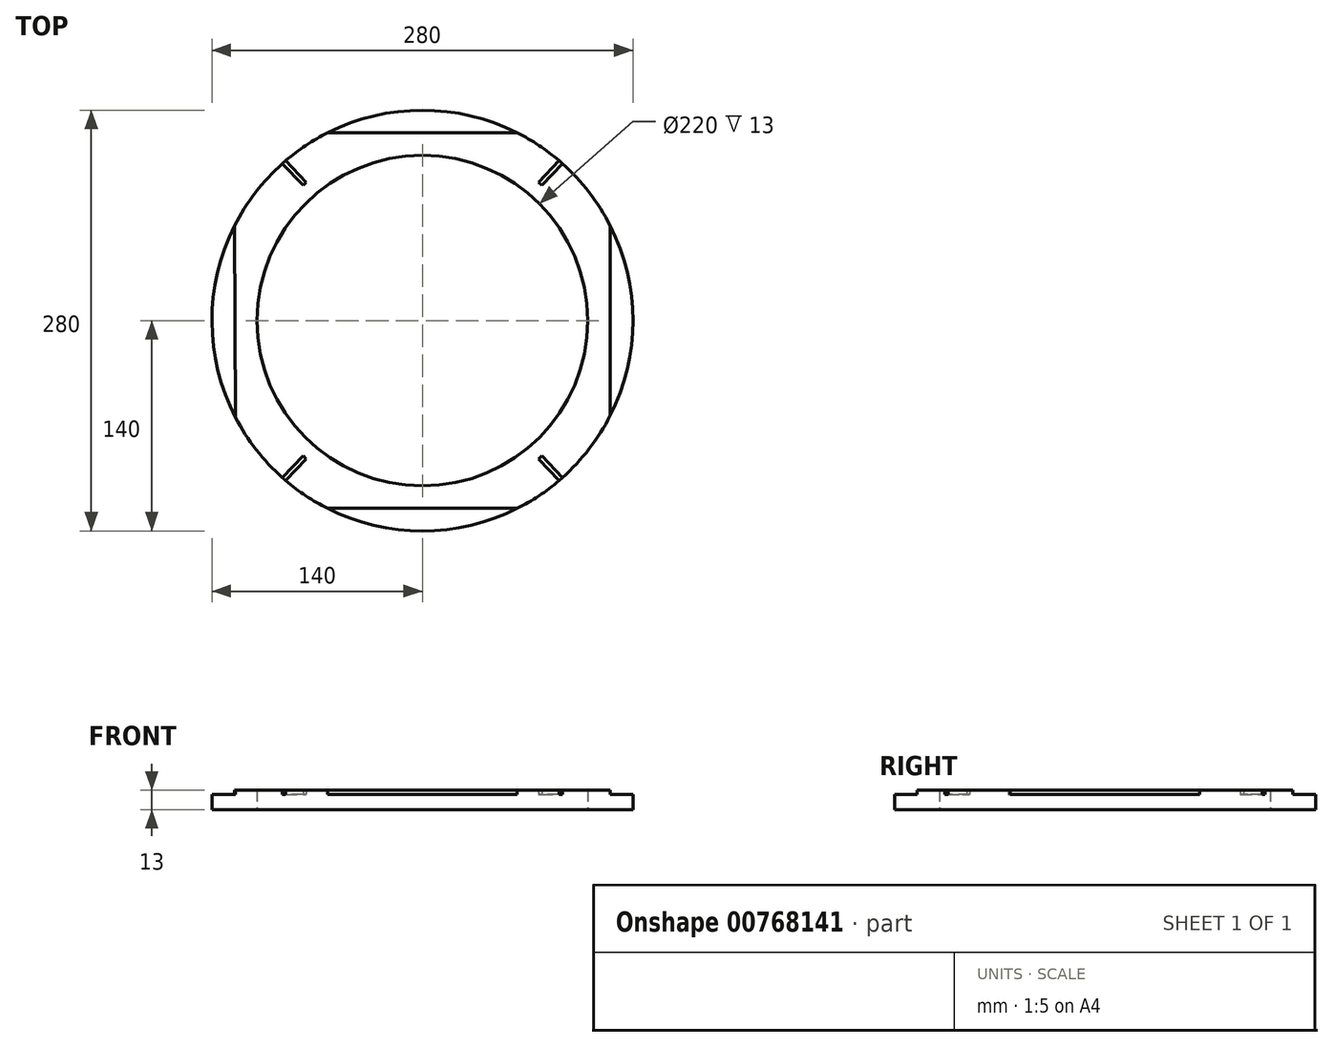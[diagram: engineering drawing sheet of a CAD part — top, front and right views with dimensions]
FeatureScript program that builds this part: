
annotation { "Feature Type Name" : "Feature", "Feature Type Description" : "" }
export const myFeature = defineFeature(function(context is Context, id is Id, definition is map)
    precondition{}
    {
        {
            var Q0;
            Q0=qCreatedBy(makeId("Top.planeOp"),FACE);
            var sketch = newSketch(context, id + "F0", { "sketchPlane" : qUnion([Q0])});
            skCircle(sketch, "E0", {"center": v(0, 0) * mm, "radius": 140 * mm});
            skCircle(sketch, "E1", {"center": v(0, 0) * mm, "radius": 110 * mm});
            skLineSegment(sketch, "E2", {"start": v(-93.13, 104.53) * mm, "end": v(-79.37, 90.02) * mm});
            skLineSegment(sketch, "E3", {"start": v(-79.37, 90.02) * mm, "end": v(-77.2, 92.08) * mm});
            skLineSegment(sketch, "E4", {"start": v(-77.2, 92.08) * mm, "end": v(-90.87, 106.5) * mm});
            skLineSegment(sketch, "E5", {"start": v(-90.87, 106.5) * mm, "end": v(-93.13, 104.53) * mm});
            skLineSegment(sketch, "E6.MirrorCS", {"start": v(-77.2, -92.08) * mm, "end": v(-90.87, -106.5) * mm});
            skLineSegment(sketch, "E7.MirrorCS", {"start": v(-79.37, -90.02) * mm, "end": v(-77.2, -92.08) * mm});
            skLineSegment(sketch, "E8.MirrorCS", {"start": v(-90.87, -106.5) * mm, "end": v(-93.13, -104.53) * mm});
            skLineSegment(sketch, "E9.MirrorCS", {"start": v(-93.13, -104.53) * mm, "end": v(-79.37, -90.02) * mm});
            skLineSegment(sketch, "E10.MirrorCS", {"start": v(90.87, -106.5) * mm, "end": v(93.13, -104.53) * mm});
            skLineSegment(sketch, "E11.MirrorCS", {"start": v(79.37, -90.02) * mm, "end": v(77.2, -92.08) * mm});
            skLineSegment(sketch, "E12.MirrorCS", {"start": v(90.87, 106.5) * mm, "end": v(93.13, 104.53) * mm});
            skLineSegment(sketch, "E13.MirrorCS", {"start": v(79.37, 90.02) * mm, "end": v(77.2, 92.08) * mm});
            skLineSegment(sketch, "E14.MirrorCS", {"start": v(77.2, -92.08) * mm, "end": v(90.87, -106.5) * mm});
            skLineSegment(sketch, "E15.MirrorCS", {"start": v(77.2, 92.08) * mm, "end": v(90.87, 106.5) * mm});
            skLineSegment(sketch, "E16.MirrorCS", {"start": v(93.13, 104.53) * mm, "end": v(79.37, 90.02) * mm});
            skLineSegment(sketch, "E17.MirrorCS", {"start": v(93.13, -104.53) * mm, "end": v(79.37, -90.02) * mm});
            skLineSegment(sketch, "E18", {"start": v(0, 140) * mm, "end": v(0, 110) * mm});
            skLineSegment(sketch, "E19", {"start": v(110, 0) * mm, "end": v(140, 0) * mm});
            skLineSegment(sketch, "E20", {"start": v(-110, 0) * mm, "end": v(-140, 0) * mm});
            skLineSegment(sketch, "E21", {"start": v(0, -110) * mm, "end": v(0, -140) * mm});
            skLineSegment(sketch, "E22", {"start": v(0, 125) * mm, "end": v(63.05, 125) * mm});
            skLineSegment(sketch, "E23", {"start": v(63.05, 125) * mm, "end": v(-63.05, 125) * mm});
            skLineSegment(sketch, "E24", {"start": v(-125, 0) * mm, "end": v(-125, 63.05) * mm});
            skLineSegment(sketch, "E25", {"start": v(-125, 63.05) * mm, "end": v(-124.29, -64.44) * mm});
            skLineSegment(sketch, "E26", {"start": v(0, -125) * mm, "end": v(63.05, -125) * mm});
            skLineSegment(sketch, "E27", {"start": v(63.05, -125) * mm, "end": v(-63.05, -125) * mm});
            skLineSegment(sketch, "E28", {"start": v(125, 0) * mm, "end": v(125, 63.05) * mm});
            skLineSegment(sketch, "E29", {"start": v(125, 63.05) * mm, "end": v(125, -63.05) * mm});
            skSolve(sketch);
        }
        {
            var Q0;
            Q0=makeQuery(id+"F0.imprint","IMPRINT",FACE,{"disambiguationData":[TD([[makeQuery(id+"F0.imprint","IMPRINT",EDGE,{"derivedFrom":sQuery(id+"F0.wireOp",EDGE,"E1")}),-1.0]])]});
            extrude(context, id + "F1", {"entities" : qUnion([Q0]), "depth" : 3 * mm, "offsetDistance" : 25.4 * mm});
        }
        {
            var Q0;
            Q0 = qSketchRegion(id + "F0", true);
            var Q1;
            Q1=makeQuery(id+"F1.opExtrude","CAP_FACE",FACE,{"disambiguationData":[OSD([sQuery(id+"F0.wireOp",EDGE,"E0"),sQuery(id+"F0.wireOp",EDGE,"E1"),sQuery(id+"F0.wireOp",EDGE,"E2"),sQuery(id+"F0.wireOp",EDGE,"E3"),sQuery(id+"F0.wireOp",EDGE,"E4"),sQuery(id+"F0.wireOp",EDGE,"E7.MirrorCS"),sQuery(id+"F0.wireOp",EDGE,"E9.MirrorCS"),sQuery(id+"F0.wireOp",EDGE,"E6.MirrorCS"),sQuery(id+"F0.wireOp",EDGE,"E13.MirrorCS"),sQuery(id+"F0.wireOp",EDGE,"E11.MirrorCS"),sQuery(id+"F0.wireOp",EDGE,"E15.MirrorCS"),sQuery(id+"F0.wireOp",EDGE,"E17.MirrorCS"),sQuery(id+"F0.wireOp",EDGE,"E16.MirrorCS"),sQuery(id+"F0.wireOp",EDGE,"E14.MirrorCS"),sQuery(id+"F0.wireOp",EDGE,"E23"),sQuery(id+"F0.wireOp",EDGE,"E25"),sQuery(id+"F0.wireOp",EDGE,"E27"),sQuery(id+"F0.wireOp",EDGE,"E29")])],"isStart":false});
            extrude(context, id + "F2", {"entities" : qUnion([Q0, Q1]), "operationType" : NewBodyOperationType.ADD, "depth" : 10 * mm, "offsetDistance" : 25.4 * mm});
        }
    });
